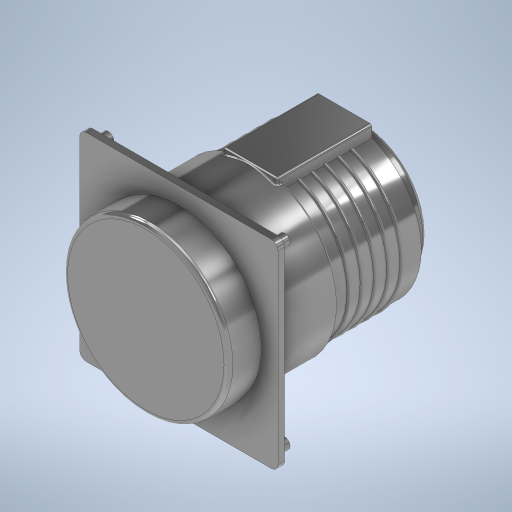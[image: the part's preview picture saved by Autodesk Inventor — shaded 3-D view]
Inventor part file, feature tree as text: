
AUTODESK INVENTOR PART (.ipt)
format: ipt  version: 2023 (Build 270158000, 158)  size: 486,912 bytes
history: native  units: mm
features: sketch x11, other x9, extrude x6, fillet x4, sweep x1, loft x1
ambient origin geometry x8: Origin, YZ Plane, XZ Plane, XY Plane, X Axis, Y Axis, Z Axis, Center Point
bodies: Body1 (feature_tree)
feature tree (32):
  other  "솔리드1"
  extrude  "돌출1"  Depth=75.0mm
  extrude  "돌출2"  Depth=50.0mm TaperAngle=0.0deg
  extrude  "돌출3"  Depth=70.0mm
  sketch  "스케치4"
  sketch  "3D 스케치1"
  other  "작업 평면2"
  fillet  "모깎기4"  Radius=40.0mm
  other  "작업 평면3"
  sweep  "스윕2"
  other  "작업 평면4"
  sketch  "스케치8"
  extrude  "돌출5"  Depth=7.0mm TaperAngle=0.0deg
  extrude  "돌출6"  Depth=7.0mm
  other  "작업 평면5"
  extrude  "돌출7"  Depth=5.0mm
  fillet  "모깎기6"  Radius=5.0mm
  other  "작업 평면7"
  sketch  "스케치10"
  other  "작업 평면6"
  other  "작업 평면8"
  loft  "로프트1"
  fillet  "모깎기7"  Radius=5.0mm
  fillet  "모깎기8"  Radius=219.911mm
  sketch  "스케치1"
  sketch  "스케치2"
  sketch  "스케치3"
  other  "곡면에 투영1"
  sketch  "스케치7"
  sketch  "스케치9"
  sketch  "스케치11"
  sketch  "스케치12"
